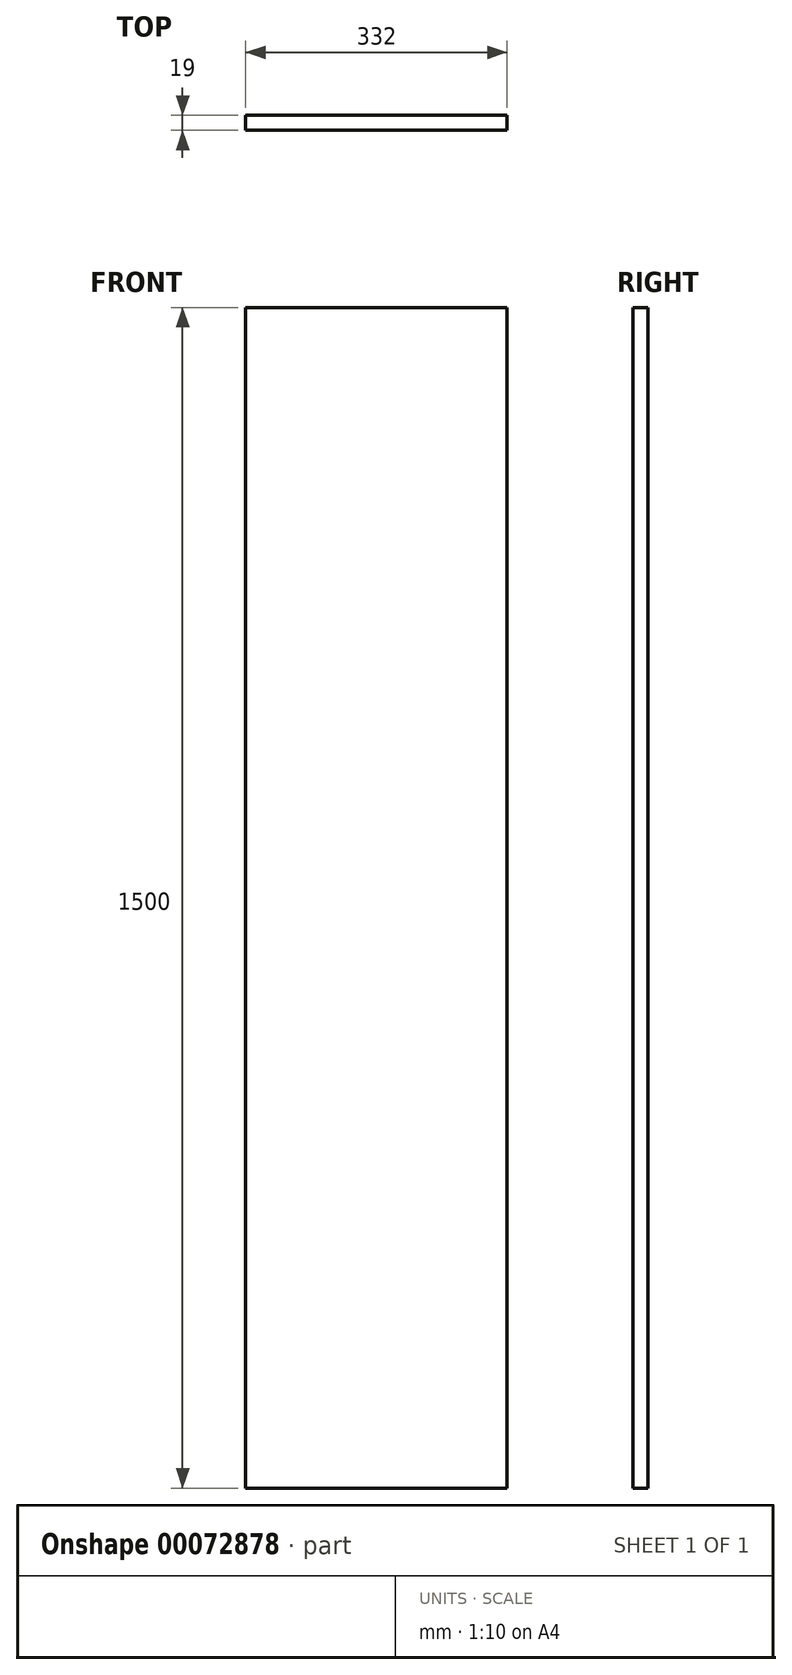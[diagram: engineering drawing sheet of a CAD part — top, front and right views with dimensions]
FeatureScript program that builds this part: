
annotation { "Feature Type Name" : "Feature", "Feature Type Description" : "" }
export const myFeature = defineFeature(function(context is Context, id is Id, definition is map)
    precondition{}
    {
        {
            var Q0;
            Q0=qCreatedBy(makeId("Front.planeOp"),FACE);
            var sketch = newSketch(context, id + "F0", { "sketchPlane" : qUnion([Q0])});
            skLineSegment(sketch, "E0.bottom", {"start": v(0, 0) * mm, "end": v(332, 0) * mm});
            skLineSegment(sketch, "E0.top", {"start": v(0, -1500) * mm, "end": v(332, -1500) * mm});
            skLineSegment(sketch, "E0.left", {"start": v(0, 0) * mm, "end": v(0, -1500) * mm});
            skLineSegment(sketch, "E0.right", {"start": v(332, 0) * mm, "end": v(332, -1500) * mm});
            skSolve(sketch);
        }
        {
            var Q0;
            Q0=qSketchRegion(id+"F0",true);
            extrude(context, id + "F1", {"entities" : qUnion([Q0]), "depth" : 19 * mm});
        }
    });
